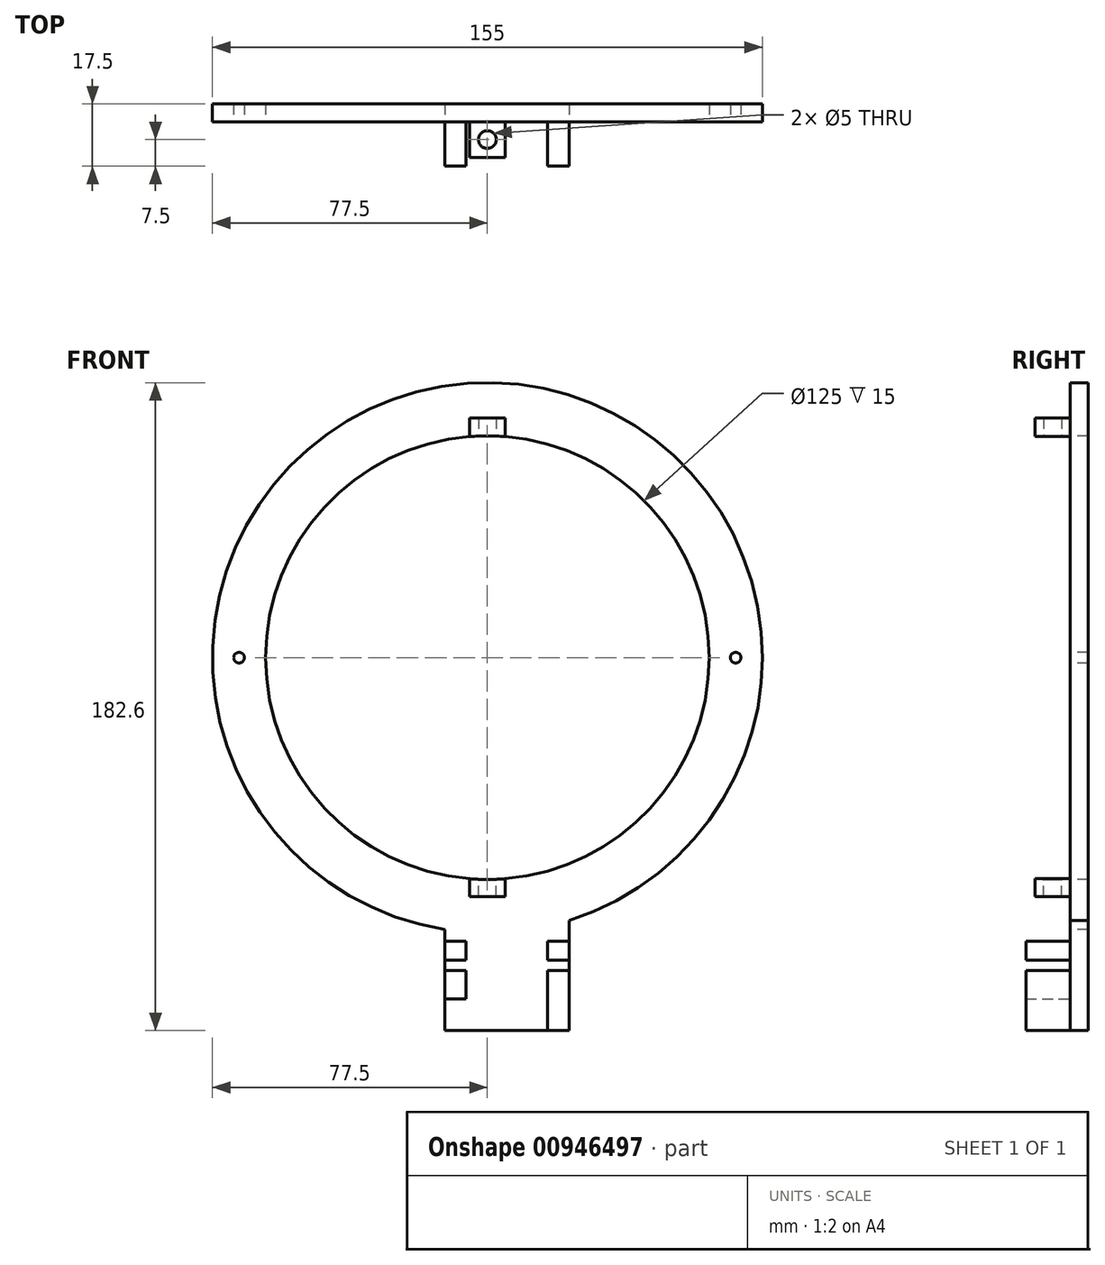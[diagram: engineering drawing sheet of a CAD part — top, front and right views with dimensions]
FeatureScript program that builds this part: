
annotation { "Feature Type Name" : "Feature", "Feature Type Description" : "" }
export const myFeature = defineFeature(function(context is Context, id is Id, definition is map)
    precondition{}
    {
        {
            var Q0;
            Q0=qCreatedBy(makeId("Front.planeOp"),FACE);
            var sketch = newSketch(context, id + "F0", { "sketchPlane" : qUnion([Q0])});
            skCircle(sketch, "E0", {"center": v(0, 0) * mm, "radius": 62.5 * mm});
            skCircle(sketch, "E1", {"center": v(0, 0) * mm, "radius": 77.5 * mm});
            skLineSegment(sketch, "E2.bottom", {"start": v(-12, -79.88) * mm, "end": v(-6, -79.88) * mm});
            skLineSegment(sketch, "E2.top", {"start": v(-12, -85.3) * mm, "end": v(-6, -85.3) * mm});
            skLineSegment(sketch, "E2.left", {"start": v(-12, -79.88) * mm, "end": v(-12, -85.3) * mm});
            skLineSegment(sketch, "E2.right", {"start": v(-6, -79.88) * mm, "end": v(-6, -85.3) * mm});
            skLineSegment(sketch, "E3.bottom", {"start": v(17, -79.88) * mm, "end": v(23, -79.88) * mm});
            skLineSegment(sketch, "E3.top", {"start": v(17, -85.3) * mm, "end": v(23, -85.3) * mm});
            skLineSegment(sketch, "E3.left", {"start": v(17, -79.88) * mm, "end": v(17, -85.3) * mm});
            skLineSegment(sketch, "E3.right", {"start": v(23, -79.88) * mm, "end": v(23, -85.3) * mm});
            skLineSegment(sketch, "E4.bottom", {"start": v(-5, -62.3) * mm, "end": v(6.33, -62.3) * mm});
            skLineSegment(sketch, "E5.bottom", {"start": v(-12, -88.1) * mm, "end": v(-6, -88.1) * mm});
            skLineSegment(sketch, "E5.top", {"start": v(-12, -96.1) * mm, "end": v(-6, -96.1) * mm});
            skLineSegment(sketch, "E5.left", {"start": v(-12, -88.1) * mm, "end": v(-12, -96.1) * mm});
            skLineSegment(sketch, "E5.right", {"start": v(-6, -88.1) * mm, "end": v(-6, -96.1) * mm});
            skLineSegment(sketch, "E6.bottom", {"start": v(17, -88.1) * mm, "end": v(23, -88.1) * mm});
            skLineSegment(sketch, "E6.top", {"start": v(17, -105.1) * mm, "end": v(23, -105.1) * mm});
            skLineSegment(sketch, "E6.left", {"start": v(17, -88.1) * mm, "end": v(17, -105.1) * mm});
            skLineSegment(sketch, "E6.right", {"start": v(23, -88.1) * mm, "end": v(23, -105.1) * mm});
            skLineSegment(sketch, "E7.bottom", {"start": v(-5, -62.3) * mm, "end": v(5, -62.3) * mm});
            skLineSegment(sketch, "E7.top", {"start": v(-5, -67.3) * mm, "end": v(5, -67.3) * mm});
            skLineSegment(sketch, "E7.left", {"start": v(-5, -62.3) * mm, "end": v(-5, -67.3) * mm});
            skLineSegment(sketch, "E7.right", {"start": v(5, -62.3) * mm, "end": v(5, -67.3) * mm});
            skPoint(sketch, "E7.middle", {"position": v(0, -64.8) * mm});
            skPoint(sketch, "E7.middle.positionSnap0", {"position": v(0.25, -64.8) * mm});
            skPoint(sketch, "E7.centerSnap0", {"position": v(0.25, -64.8) * mm});
            skLineSegment(sketch, "E8.bottom", {"start": v(-5, 62.3) * mm, "end": v(5, 62.3) * mm});
            skLineSegment(sketch, "E8.top", {"start": v(-5, 67.5) * mm, "end": v(5, 67.5) * mm});
            skLineSegment(sketch, "E8.left", {"start": v(-5, 62.3) * mm, "end": v(-5, 67.5) * mm});
            skLineSegment(sketch, "E8.right", {"start": v(5, 62.3) * mm, "end": v(5, 67.5) * mm});
            skPoint(sketch, "E8.middle", {"position": v(0, 64.9) * mm});
            skLineSegment(sketch, "E9.bottom", {"start": v(23, -105.1) * mm, "end": v(-12, -105.1) * mm});
            skLineSegment(sketch, "E9.top", {"start": v(23, -63.72) * mm, "end": v(-12, -63.72) * mm});
            skLineSegment(sketch, "E9.left", {"start": v(23, -105.1) * mm, "end": v(23, -63.72) * mm});
            skLineSegment(sketch, "E9.right", {"start": v(-12, -105.1) * mm, "end": v(-12, -63.72) * mm});
            skPoint(sketch, "E10", {"position": v(-70, 0) * mm});
            skPoint(sketch, "E11", {"position": v(70, 0) * mm});
            skSolve(sketch);
        }
        {
            var Q0;
            Q0=makeQuery(id+"F0.imprint","IMPRINT",FACE,{"disambiguationData":[TD([[makeQuery(id+"F0.imprint","IMPRINT",EDGE,{"derivedFrom":sQuery(id+"F0.wireOp",EDGE,"E8.top")}),1.0]])]});
            var Q1;
            {var subQ12=sQuery(id+"F0.wireOp",EDGE,"E2.bottom");Q1=makeQuery(id+"F0.imprint","IMPRINT",FACE,{"disambiguationData":[TD([[makeQuery(id+"F0.imprint","IMPRINT",EDGE,{"derivedFrom":subQ12}),1.0]])]});}
            var Q2;
            {var subQ1=sQuery(id+"F0.wireOp",EDGE,"E7.top");Q2=makeQuery(id+"F0.imprint","IMPRINT",FACE,{"disambiguationData":[TD([[makeQuery(id+"F0.imprint","IMPRINT",EDGE,{"derivedFrom":subQ1}),-1.0]])]});}
            var Q3;
            {var subQ0=sQuery(id+"F0.wireOp",EDGE,"E3.bottom");Q3=makeQuery(id+"F0.imprint","IMPRINT",FACE,{"disambiguationData":[TD([[makeQuery(id+"F0.imprint","IMPRINT",EDGE,{"derivedFrom":subQ0}),-1.0]])]});}
            var Q4;
            {var subQ0=sQuery(id+"F0.wireOp",EDGE,"E6.bottom");Q4=makeQuery(id+"F0.imprint","IMPRINT",FACE,{"disambiguationData":[TD([[makeQuery(id+"F0.imprint","IMPRINT",EDGE,{"derivedFrom":subQ0}),-1.0]])]});}
            var Q5;
            {var subQ0=sQuery(id+"F0.wireOp",EDGE,"E2.bottom");Q5=makeQuery(id+"F0.imprint","IMPRINT",FACE,{"disambiguationData":[TD([[makeQuery(id+"F0.imprint","IMPRINT",EDGE,{"derivedFrom":subQ0}),-1.0]])]});}
            var Q6;
            {var subQ0=sQuery(id+"F0.wireOp",EDGE,"E5.bottom");Q6=makeQuery(id+"F0.imprint","IMPRINT",FACE,{"disambiguationData":[TD([[makeQuery(id+"F0.imprint","IMPRINT",EDGE,{"derivedFrom":subQ0}),-1.0]])]});}
            var Q7;
            {var subQ0=sQuery(id+"F0.wireOp",EDGE,"E7.top");Q7=makeQuery(id+"F0.imprint","IMPRINT",FACE,{"disambiguationData":[TD([[makeQuery(id+"F0.imprint","IMPRINT",EDGE,{"derivedFrom":subQ0}),1.0]])]});}
            var Q8;
            {var subQ4=sQuery(id+"F0.wireOp",EDGE,"E7.left");var subQ6=sQuery(id+"F0.wireOp",EDGE,"E9.top");var subQ7=makeQuery(id+"F0.imprint","INTERSECT",VERTEX,{"derivedFrom":[subQ4,subQ6]});Q8=makeQuery(id+"F0.imprint","IMPRINT",FACE,{"disambiguationData":[TD([[makeQuery(id+"F0.imprint","IMPRINT",EDGE,{"disambiguationData":[TD([[subQ7,1.0]])],"derivedFrom":subQ6}),-1.0]])]});}
            var Q9;
            Q9=makeQuery(id+"F0.imprint","IMPRINT",FACE,{"disambiguationData":[TD([[makeQuery(id+"F0.imprint","IMPRINT",EDGE,{"derivedFrom":sQuery(id+"F0.wireOp",EDGE,"E8.top")}),-1.0]])]});
            extrude(context, id + "F1", {"entities" : qUnion([Q0, Q1, Q2, Q3, Q4, Q5, Q6, Q7, Q8, Q9]), "depth" : -5 * mm, "offsetDistance" : 25 * mm});
        }
        {
            var Q0;
            {var subQ0=sQuery(id+"F0.wireOp",EDGE,"E3.bottom");Q0=makeQuery(id+"F0.imprint","IMPRINT",FACE,{"disambiguationData":[TD([[makeQuery(id+"F0.imprint","IMPRINT",EDGE,{"derivedFrom":subQ0}),-1.0]])]});}
            var Q1;
            {var subQ0=sQuery(id+"F0.wireOp",EDGE,"E6.bottom");Q1=makeQuery(id+"F0.imprint","IMPRINT",FACE,{"disambiguationData":[TD([[makeQuery(id+"F0.imprint","IMPRINT",EDGE,{"derivedFrom":subQ0}),-1.0]])]});}
            var Q2;
            {var subQ0=sQuery(id+"F0.wireOp",EDGE,"E5.bottom");Q2=makeQuery(id+"F0.imprint","IMPRINT",FACE,{"disambiguationData":[TD([[makeQuery(id+"F0.imprint","IMPRINT",EDGE,{"derivedFrom":subQ0}),-1.0]])]});}
            var Q3;
            {var subQ0=sQuery(id+"F0.wireOp",EDGE,"E2.bottom");Q3=makeQuery(id+"F0.imprint","IMPRINT",FACE,{"disambiguationData":[TD([[makeQuery(id+"F0.imprint","IMPRINT",EDGE,{"derivedFrom":subQ0}),-1.0]])]});}
            extrude(context, id + "F2", {"entities" : qUnion([Q0, Q1, Q2, Q3]), "depth" : 12.5 * mm, "offsetDistance" : 25 * mm});
        }
        {
            var Q0;
            Q0=makeQuery(id+"F0.imprint","IMPRINT",FACE,{"disambiguationData":[TD([[makeQuery(id+"F0.imprint","IMPRINT",EDGE,{"derivedFrom":sQuery(id+"F0.wireOp",EDGE,"E8.top")}),-1.0]])]});
            var Q1;
            {var subQ4=sQuery(id+"F0.wireOp",EDGE,"E7.left");var subQ6=sQuery(id+"F0.wireOp",EDGE,"E9.top");var subQ7=makeQuery(id+"F0.imprint","INTERSECT",VERTEX,{"derivedFrom":[subQ4,subQ6]});Q1=makeQuery(id+"F0.imprint","IMPRINT",FACE,{"disambiguationData":[TD([[makeQuery(id+"F0.imprint","IMPRINT",EDGE,{"disambiguationData":[TD([[subQ7,1.0]])],"derivedFrom":subQ6}),-1.0]])]});}
            var Q2;
            {var subQ0=sQuery(id+"F0.wireOp",EDGE,"E7.top");Q2=makeQuery(id+"F0.imprint","IMPRINT",FACE,{"disambiguationData":[TD([[makeQuery(id+"F0.imprint","IMPRINT",EDGE,{"derivedFrom":subQ0}),1.0]])]});}
            extrude(context, id + "F3", {"entities" : qUnion([Q0, Q1, Q2]), "operationType" : NewBodyOperationType.ADD, "depth" : 10 * mm, "offsetDistance" : 25 * mm});
        }
        {
            var Q0;
            Q0=qCreatedBy(makeId("Top.planeOp"),FACE);
            var sketch = newSketch(context, id + "F4", { "sketchPlane" : qUnion([Q0])});
            skLineSegment(sketch, "E12.bottom", {"start": v(-5.13, -10) * mm, "end": v(5.13, -10) * mm});
            skLineSegment(sketch, "E12.top", {"start": v(-5.13, 0) * mm, "end": v(5.13, 0) * mm});
            skLineSegment(sketch, "E12.left", {"start": v(-5.13, -10) * mm, "end": v(-5.13, 0) * mm});
            skLineSegment(sketch, "E12.right", {"start": v(5.13, -10) * mm, "end": v(5.13, 0) * mm});
            skPoint(sketch, "E12.middle", {"position": v(0, -5) * mm});
            skSolve(sketch);
        }
        {
            var Q0;
            Q0=sQuery(id+"F4.wireOp",VERTEX,"E12.middle");
            var Q1;
            Q1=makeQuery(id+"F1.opExtrude","SWEPT_BODY",BODY,{"disambiguationData":[OSD([sQuery(id+"F0.wireOp",EDGE,"E0"),sQuery(id+"F0.wireOp",EDGE,"E1"),sQuery(id+"F0.wireOp",EDGE,"E9.bottom"),sQuery(id+"F0.wireOp",EDGE,"E9.left"),sQuery(id+"F0.wireOp",EDGE,"E9.right")])]});
            hole(context, id + "F5", {"style" : HoleStyle.SIMPLE, "endStyle" : HoleEndStyle.THROUGH, "holeDiameter" : 5 * mm, "majorDiameter" : 5 * mm, "isTappedThrough" : true, "tappedDepth" : 12 * mm, "tapClearance" : 3, "locations" : qUnion([Q0]), "scope" : qUnion([Q1])});
        }
        {
            var Q0;
            Q0=sQuery(id+"F4.wireOp",VERTEX,"E12.middle");
            var Q1;
            Q1=makeQuery(id+"F1.opExtrude","SWEPT_BODY",BODY,{"disambiguationData":[OSD([sQuery(id+"F0.wireOp",EDGE,"E0"),sQuery(id+"F0.wireOp",EDGE,"E1"),sQuery(id+"F0.wireOp",EDGE,"E9.bottom"),sQuery(id+"F0.wireOp",EDGE,"E9.left"),sQuery(id+"F0.wireOp",EDGE,"E9.right")])]});
            hole(context, id + "F6", {"style" : HoleStyle.SIMPLE, "endStyle" : HoleEndStyle.THROUGH, "oppositeDirection" : true, "holeDiameter" : 5 * mm, "majorDiameter" : 5 * mm, "isTappedThrough" : true, "tappedDepth" : 12 * mm, "tapClearance" : 3, "locations" : qUnion([Q0]), "scope" : qUnion([Q1])});
        }
        {
            var Q0;
            Q0=sQuery(id+"F0.wireOp",VERTEX,"E10");
            var Q1;
            Q1=sQuery(id+"F0.wireOp",VERTEX,"E11");
            var Q2;
            Q2=makeQuery(id+"F1.opExtrude","SWEPT_BODY",BODY,{"disambiguationData":[OSD([sQuery(id+"F0.wireOp",EDGE,"E0"),sQuery(id+"F0.wireOp",EDGE,"E1"),sQuery(id+"F0.wireOp",EDGE,"E9.bottom"),sQuery(id+"F0.wireOp",EDGE,"E9.left"),sQuery(id+"F0.wireOp",EDGE,"E9.right")])]});
            hole(context, id + "F7", {"style" : HoleStyle.SIMPLE, "endStyle" : HoleEndStyle.THROUGH, "holeDiameter" : 3 * mm, "majorDiameter" : 5 * mm, "isTappedThrough" : true, "tappedDepth" : 12 * mm, "tapClearance" : 3, "locations" : qUnion([Q0, Q1]), "scope" : qUnion([Q2])});
        }
    });
